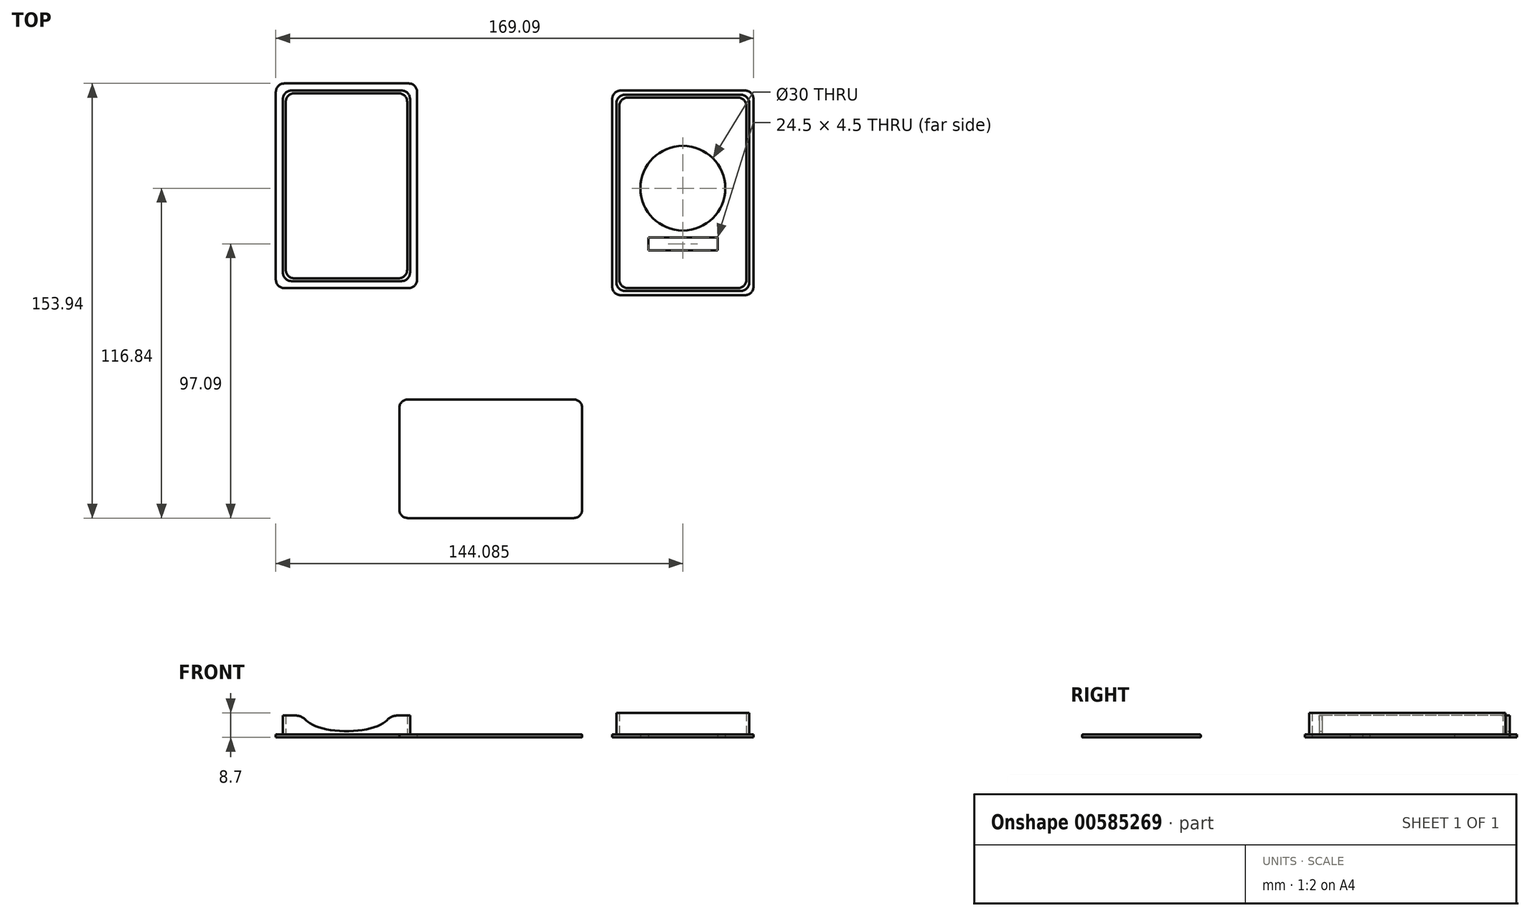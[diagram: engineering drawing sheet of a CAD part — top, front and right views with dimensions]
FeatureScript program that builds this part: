
annotation { "Feature Type Name" : "Feature", "Feature Type Description" : "" }
export const myFeature = defineFeature(function(context is Context, id is Id, definition is map)
    precondition{}
    {
        {
            var Q0;
            Q0=qCreatedBy(makeId("Top.planeOp"),FACE);
            var sketch = newSketch(context, id + "F0", { "sketchPlane" : qUnion([Q0])});
            skLineSegment(sketch, "E0.bottom", {"start": v(-88.15, 72.5) * mm, "end": v(-38.15, 72.5) * mm});
            skLineSegment(sketch, "E0.top", {"start": v(-88.15, 0) * mm, "end": v(-38.15, 0) * mm});
            skLineSegment(sketch, "E0.left", {"start": v(-88.15, 72.5) * mm, "end": v(-88.15, 0) * mm});
            skLineSegment(sketch, "E0.right", {"start": v(-38.15, 72.5) * mm, "end": v(-38.15, 0) * mm});
            skLineSegment(sketch, "E1.bottom", {"start": v(33.44, 67.5) * mm, "end": v(78.44, 67.5) * mm});
            skLineSegment(sketch, "E1.top", {"start": v(33.44, 0) * mm, "end": v(78.44, 0) * mm});
            skLineSegment(sketch, "E1.left", {"start": v(33.44, 67.5) * mm, "end": v(33.44, 0) * mm});
            skLineSegment(sketch, "E1.right", {"start": v(78.44, 67.5) * mm, "end": v(78.44, 0) * mm});
            skLineSegment(sketch, "E2.bottom", {"start": v(-44.44, -39.44) * mm, "end": v(20.3, -39.44) * mm});
            skLineSegment(sketch, "E2.top", {"start": v(-44.44, -81.44) * mm, "end": v(20.3, -81.44) * mm});
            skLineSegment(sketch, "E2.left", {"start": v(-44.44, -39.44) * mm, "end": v(-44.44, -81.44) * mm});
            skLineSegment(sketch, "E2.right", {"start": v(20.3, -39.44) * mm, "end": v(20.3, -81.44) * mm});
            skLineSegment(sketch, "E3.bottom", {"start": v(-40.65, 70) * mm, "end": v(-85.65, 70) * mm});
            skLineSegment(sketch, "E3.top", {"start": v(-40.65, 2.5) * mm, "end": v(-85.65, 2.5) * mm});
            skLineSegment(sketch, "E3.left", {"start": v(-40.65, 70) * mm, "end": v(-40.65, 2.5) * mm});
            skLineSegment(sketch, "E3.right", {"start": v(-85.65, 70) * mm, "end": v(-85.65, 2.5) * mm});
            skPoint(sketch, "E3.middle", {"position": v(-63.15, 36.25) * mm});
            skPoint(sketch, "E3.middle.positionSnap0", {"position": v(-88.15, 36.25) * mm});
            skPoint(sketch, "E3.middle.positionSnap1", {"position": v(-63.15, 72.5) * mm});
            skPoint(sketch, "E3.centerSnap0", {"position": v(-88.15, 36.25) * mm});
            skPoint(sketch, "E3.centerSnap1", {"position": v(-63.15, 72.5) * mm});
            skLineSegment(sketch, "E4.bottom", {"start": v(-41.65, 69) * mm, "end": v(-84.65, 69) * mm});
            skLineSegment(sketch, "E4.top", {"start": v(-41.65, 3.5) * mm, "end": v(-84.65, 3.5) * mm});
            skLineSegment(sketch, "E4.left", {"start": v(-41.65, 69) * mm, "end": v(-41.65, 3.5) * mm});
            skLineSegment(sketch, "E4.right", {"start": v(-84.65, 69) * mm, "end": v(-84.65, 3.5) * mm});
            skLineSegment(sketch, "E5.bottom", {"start": v(32.44, 68.5) * mm, "end": v(79.44, 68.5) * mm});
            skLineSegment(sketch, "E5.top", {"start": v(32.44, -1) * mm, "end": v(79.44, -1) * mm});
            skLineSegment(sketch, "E5.left", {"start": v(32.44, 68.5) * mm, "end": v(32.44, -1) * mm});
            skLineSegment(sketch, "E5.right", {"start": v(79.44, 68.5) * mm, "end": v(79.44, -1) * mm});
            skPoint(sketch, "E5.middle", {"position": v(55.94, 33.75) * mm});
            skPoint(sketch, "E5.middle.positionSnap0", {"position": v(55.94, 67.5) * mm});
            skPoint(sketch, "E5.middle.positionSnap1", {"position": v(33.44, 33.75) * mm});
            skPoint(sketch, "E5.centerSnap0", {"position": v(55.94, 67.5) * mm});
            skPoint(sketch, "E5.centerSnap1", {"position": v(33.44, 33.75) * mm});
            skLineSegment(sketch, "E6.bottom", {"start": v(80.94, -2.5) * mm, "end": v(30.94, -2.5) * mm});
            skLineSegment(sketch, "E6.top", {"start": v(80.94, 70) * mm, "end": v(30.94, 70) * mm});
            skLineSegment(sketch, "E6.left", {"start": v(80.94, -2.5) * mm, "end": v(80.94, 70) * mm});
            skLineSegment(sketch, "E6.right", {"start": v(30.94, -2.5) * mm, "end": v(30.94, 70) * mm});
            skCircle(sketch, "E7", {"center": v(55.94, 35.4) * mm, "radius": 15 * mm});
            skLineSegment(sketch, "E8.bottom", {"start": v(68.19, 17.9) * mm, "end": v(43.69, 17.9) * mm});
            skLineSegment(sketch, "E8.top", {"start": v(68.19, 13.4) * mm, "end": v(43.69, 13.4) * mm});
            skLineSegment(sketch, "E8.left", {"start": v(68.19, 17.9) * mm, "end": v(68.19, 13.4) * mm});
            skLineSegment(sketch, "E8.right", {"start": v(43.69, 17.9) * mm, "end": v(43.69, 13.4) * mm});
            skPoint(sketch, "E8.middle", {"position": v(55.94, 15.65) * mm});
            skSolve(sketch);
        }
        {
            var Q0;
            Q0=makeQuery(id+"F0.imprint","IMPRINT",FACE,{"disambiguationData":[TD([[makeQuery(id+"F0.imprint","IMPRINT",EDGE,{"derivedFrom":sQuery(id+"F0.wireOp",EDGE,"E2.bottom")}),-1.0]])]});
            extrude(context, id + "F1", {"entities" : qUnion([Q0]), "depth" : 1 * mm, "offsetDistance" : 25 * mm});
        }
        {
            var Q0;
            Q0=makeQuery(id+"F1.opExtrude","SWEPT_EDGE",EDGE,{"disambiguationData":[OSD([sQuery(id+"F0.wireOp",EDGE,"E2.bottom"),sQuery(id+"F0.wireOp",EDGE,"E2.left")])]});
            var Q1;
            Q1=makeQuery(id+"F1.opExtrude","SWEPT_EDGE",EDGE,{"disambiguationData":[OSD([sQuery(id+"F0.wireOp",EDGE,"E2.top"),sQuery(id+"F0.wireOp",EDGE,"E2.left")])]});
            var Q2;
            Q2=makeQuery(id+"F1.opExtrude","SWEPT_EDGE",EDGE,{"disambiguationData":[OSD([sQuery(id+"F0.wireOp",EDGE,"E2.top"),sQuery(id+"F0.wireOp",EDGE,"E2.right")])]});
            var Q3;
            Q3=makeQuery(id+"F1.opExtrude","SWEPT_EDGE",EDGE,{"disambiguationData":[OSD([sQuery(id+"F0.wireOp",EDGE,"E2.bottom"),sQuery(id+"F0.wireOp",EDGE,"E2.right")])]});
            fillet(context, id + "F2", {"entities" : qUnion([Q0, Q1, Q2, Q3]), "radius" : 3 * mm, "tangentPropagation" : true, "allowEdgeOverflow" : false});
        }
        {
            var Q0;
            Q0=makeQuery(id+"F1.opExtrude","CAP_FACE",FACE,{"disambiguationData":[OSD([sQuery(id+"F0.wireOp",EDGE,"E2.bottom"),sQuery(id+"F0.wireOp",EDGE,"E2.top"),sQuery(id+"F0.wireOp",EDGE,"E2.left"),sQuery(id+"F0.wireOp",EDGE,"E2.right")])],"isStart":false});
            var Q1;
            Q1=makeQuery(id+"F1.opExtrude","CAP_FACE",FACE,{"disambiguationData":[OSD([sQuery(id+"F0.wireOp",EDGE,"E2.bottom"),sQuery(id+"F0.wireOp",EDGE,"E2.top"),sQuery(id+"F0.wireOp",EDGE,"E2.left"),sQuery(id+"F0.wireOp",EDGE,"E2.right")])],"isStart":true});
            fillet(context, id + "F3", {"entities" : qUnion([Q0, Q1]), "radius" : 0.2 * mm, "tangentPropagation" : true, "allowEdgeOverflow" : false});
        }
        {
            var Q0;
            Q0=makeQuery(id+"F0.imprint","IMPRINT",FACE,{"disambiguationData":[TD([[makeQuery(id+"F0.imprint","IMPRINT",EDGE,{"derivedFrom":sQuery(id+"F0.wireOp",EDGE,"E0.bottom")}),-1.0]])]});
            var Q1;
            Q1=makeQuery(id+"F0.imprint","IMPRINT",FACE,{"disambiguationData":[TD([[makeQuery(id+"F0.imprint","IMPRINT",EDGE,{"derivedFrom":sQuery(id+"F0.wireOp",EDGE,"E3.bottom")}),1.0]])]});
            var Q2;
            Q2=makeQuery(id+"F0.imprint","IMPRINT",FACE,{"disambiguationData":[TD([[makeQuery(id+"F0.imprint","IMPRINT",EDGE,{"derivedFrom":sQuery(id+"F0.wireOp",EDGE,"E4.bottom")}),1.0]])]});
            extrude(context, id + "F4", {"entities" : qUnion([Q0, Q1, Q2]), "depth" : 1 * mm, "offsetDistance" : 25 * mm});
        }
        {
            var Q0;
            Q0=makeQuery(id+"F0.imprint","IMPRINT",FACE,{"disambiguationData":[TD([[makeQuery(id+"F0.imprint","IMPRINT",EDGE,{"derivedFrom":sQuery(id+"F0.wireOp",EDGE,"E3.bottom")}),1.0]])]});
            extrude(context, id + "F5", {"entities" : qUnion([Q0]), "operationType" : NewBodyOperationType.ADD, "depth" : 7.75 * mm, "offsetDistance" : 25 * mm});
        }
        {
            var Q0;
            Q0=makeQuery(id+"F5.opExtrude","SWEPT_EDGE",EDGE,{"disambiguationData":[OSD([sQuery(id+"F0.wireOp",EDGE,"E3.top"),sQuery(id+"F0.wireOp",EDGE,"E3.right")])]});
            var Q1;
            Q1=makeQuery(id+"F5.opExtrude","SWEPT_EDGE",EDGE,{"disambiguationData":[OSD([sQuery(id+"F0.wireOp",EDGE,"E3.top"),sQuery(id+"F0.wireOp",EDGE,"E3.left")])]});
            var Q2;
            Q2=makeQuery(id+"F5.opExtrude","SWEPT_EDGE",EDGE,{"disambiguationData":[OSD([sQuery(id+"F0.wireOp",EDGE,"E3.bottom"),sQuery(id+"F0.wireOp",EDGE,"E3.right")])]});
            var Q3;
            Q3=makeQuery(id+"F5.opExtrude","SWEPT_EDGE",EDGE,{"disambiguationData":[OSD([sQuery(id+"F0.wireOp",EDGE,"E3.bottom"),sQuery(id+"F0.wireOp",EDGE,"E3.left")])]});
            var Q4;
            Q4=makeQuery(id+"F4.opExtrude","SWEPT_EDGE",EDGE,{"disambiguationData":[OSD([sQuery(id+"F0.wireOp",EDGE,"E0.bottom"),sQuery(id+"F0.wireOp",EDGE,"E0.left")])]});
            var Q5;
            Q5=makeQuery(id+"F4.opExtrude","SWEPT_EDGE",EDGE,{"disambiguationData":[OSD([sQuery(id+"F0.wireOp",EDGE,"E0.bottom"),sQuery(id+"F0.wireOp",EDGE,"E0.right")])]});
            var Q6;
            Q6=makeQuery(id+"F4.opExtrude","SWEPT_EDGE",EDGE,{"disambiguationData":[OSD([sQuery(id+"F0.wireOp",EDGE,"E0.top"),sQuery(id+"F0.wireOp",EDGE,"E0.right")])]});
            var Q7;
            Q7=makeQuery(id+"F4.opExtrude","SWEPT_EDGE",EDGE,{"disambiguationData":[OSD([sQuery(id+"F0.wireOp",EDGE,"E0.top"),sQuery(id+"F0.wireOp",EDGE,"E0.left")])]});
            var Q8;
            Q8=makeQuery(id+"F5.opExtrude","SWEPT_EDGE",EDGE,{"disambiguationData":[OSD([sQuery(id+"F0.wireOp",EDGE,"E4.top"),sQuery(id+"F0.wireOp",EDGE,"E4.left")])]});
            var Q9;
            Q9=makeQuery(id+"F5.opExtrude","SWEPT_EDGE",EDGE,{"disambiguationData":[OSD([sQuery(id+"F0.wireOp",EDGE,"E4.top"),sQuery(id+"F0.wireOp",EDGE,"E4.right")])]});
            var Q10;
            Q10=makeQuery(id+"F5.opExtrude","SWEPT_EDGE",EDGE,{"disambiguationData":[OSD([sQuery(id+"F0.wireOp",EDGE,"E4.bottom"),sQuery(id+"F0.wireOp",EDGE,"E4.right")])]});
            var Q11;
            Q11=makeQuery(id+"F5.opExtrude","SWEPT_EDGE",EDGE,{"disambiguationData":[OSD([sQuery(id+"F0.wireOp",EDGE,"E4.bottom"),sQuery(id+"F0.wireOp",EDGE,"E4.left")])]});
            fillet(context, id + "F6", {"entities" : qUnion([Q0, Q1, Q2, Q3, Q4, Q5, Q6, Q7, Q8, Q9, Q10, Q11]), "radius" : 3 * mm, "tangentPropagation" : true, "allowEdgeOverflow" : false});
        }
        {
            var Q0;
            Q0=makeQuery(id+"F5.opExtrude","SWEPT_FACE",FACE,{"disambiguationData":[OSD([sQuery(id+"F0.wireOp",EDGE,"E3.top")])]});
            var sketch = newSketch(context, id + "F7", { "sketchPlane" : qUnion([Q0])});
            skEllipse(sketch, "E9", {"center": v(-63.15, 7.75) * mm, "majorRadius": 15 * mm, "minorRadius": 5.5 * mm, "majorAxis": v(1, 0)});
            skSolve(sketch);
        }
        {
            var Q0;
            Q0 = qSketchRegion(id + "F7", true);
            extrude(context, id + "F8", {"entities" : qUnion([Q0]), "operationType" : NewBodyOperationType.REMOVE, "endBound" : BoundingType.THROUGH_ALL, "oppositeDirection" : true, "depth" : 25 * mm, "offsetDistance" : 25 * mm});
        }
        {
            var Q0;
            Q0=makeQuery(id+"F8.boolean.opBoolean","INTERSECT",EDGE,{"disambiguationData":[OD(1.0)],"derivedFrom":[makeQuery(id+"F5.opExtrude","CAP_FACE",FACE,{"disambiguationData":[OSD([sQuery(id+"F0.wireOp",EDGE,"E3.bottom"),sQuery(id+"F0.wireOp",EDGE,"E3.top"),sQuery(id+"F0.wireOp",EDGE,"E3.left"),sQuery(id+"F0.wireOp",EDGE,"E3.right"),sQuery(id+"F0.wireOp",EDGE,"E4.bottom"),sQuery(id+"F0.wireOp",EDGE,"E4.top"),sQuery(id+"F0.wireOp",EDGE,"E4.left"),sQuery(id+"F0.wireOp",EDGE,"E4.right")])],"isStart":false}),makeQuery(id+"F8.opExtrude","SWEPT_FACE",FACE,{"disambiguationData":[OSD([sQuery(id+"F7.wireOp",EDGE,"E9")])]})]});
            var Q1;
            Q1=makeQuery(id+"F8.boolean.opBoolean","INTERSECT",EDGE,{"disambiguationData":[OD(3.0)],"derivedFrom":[makeQuery(id+"F5.opExtrude","CAP_FACE",FACE,{"disambiguationData":[OSD([sQuery(id+"F0.wireOp",EDGE,"E3.bottom"),sQuery(id+"F0.wireOp",EDGE,"E3.top"),sQuery(id+"F0.wireOp",EDGE,"E3.left"),sQuery(id+"F0.wireOp",EDGE,"E3.right"),sQuery(id+"F0.wireOp",EDGE,"E4.bottom"),sQuery(id+"F0.wireOp",EDGE,"E4.top"),sQuery(id+"F0.wireOp",EDGE,"E4.left"),sQuery(id+"F0.wireOp",EDGE,"E4.right")])],"isStart":false}),makeQuery(id+"F8.opExtrude","SWEPT_FACE",FACE,{"disambiguationData":[OSD([sQuery(id+"F7.wireOp",EDGE,"E9")])]})]});
            var Q2;
            Q2=makeQuery(id+"F8.boolean.opBoolean","INTERSECT",EDGE,{"disambiguationData":[OD(0.0)],"derivedFrom":[makeQuery(id+"F5.opExtrude","CAP_FACE",FACE,{"disambiguationData":[OSD([sQuery(id+"F0.wireOp",EDGE,"E3.bottom"),sQuery(id+"F0.wireOp",EDGE,"E3.top"),sQuery(id+"F0.wireOp",EDGE,"E3.left"),sQuery(id+"F0.wireOp",EDGE,"E3.right"),sQuery(id+"F0.wireOp",EDGE,"E4.bottom"),sQuery(id+"F0.wireOp",EDGE,"E4.top"),sQuery(id+"F0.wireOp",EDGE,"E4.left"),sQuery(id+"F0.wireOp",EDGE,"E4.right")])],"isStart":false}),makeQuery(id+"F8.opExtrude","SWEPT_FACE",FACE,{"disambiguationData":[OSD([sQuery(id+"F7.wireOp",EDGE,"E9")])]})]});
            var Q3;
            Q3=makeQuery(id+"F8.boolean.opBoolean","INTERSECT",EDGE,{"disambiguationData":[OD(2.0)],"derivedFrom":[makeQuery(id+"F5.opExtrude","CAP_FACE",FACE,{"disambiguationData":[OSD([sQuery(id+"F0.wireOp",EDGE,"E3.bottom"),sQuery(id+"F0.wireOp",EDGE,"E3.top"),sQuery(id+"F0.wireOp",EDGE,"E3.left"),sQuery(id+"F0.wireOp",EDGE,"E3.right"),sQuery(id+"F0.wireOp",EDGE,"E4.bottom"),sQuery(id+"F0.wireOp",EDGE,"E4.top"),sQuery(id+"F0.wireOp",EDGE,"E4.left"),sQuery(id+"F0.wireOp",EDGE,"E4.right")])],"isStart":false}),makeQuery(id+"F8.opExtrude","SWEPT_FACE",FACE,{"disambiguationData":[OSD([sQuery(id+"F7.wireOp",EDGE,"E9")])]})]});
            fillet(context, id + "F9", {"entities" : qUnion([Q0, Q1, Q2, Q3]), "radius" : 5 * mm, "tangentPropagation" : true, "allowEdgeOverflow" : false});
        }
        {
            var Q0;
            Q0=makeQuery(id+"F0.imprint","IMPRINT",FACE,{"disambiguationData":[TD([[makeQuery(id+"F0.imprint","IMPRINT",EDGE,{"derivedFrom":sQuery(id+"F0.wireOp",EDGE,"E5.bottom")}),1.0]])]});
            var Q1;
            Q1=makeQuery(id+"F0.imprint","IMPRINT",FACE,{"disambiguationData":[TD([[makeQuery(id+"F0.imprint","IMPRINT",EDGE,{"derivedFrom":sQuery(id+"F0.wireOp",EDGE,"E1.bottom")}),1.0]])]});
            var Q2;
            Q2=makeQuery(id+"F0.imprint","IMPRINT",FACE,{"disambiguationData":[TD([[makeQuery(id+"F0.imprint","IMPRINT",EDGE,{"derivedFrom":sQuery(id+"F0.wireOp",EDGE,"E1.bottom")}),-1.0]])]});
            extrude(context, id + "F10", {"entities" : qUnion([Q0, Q1, Q2]), "depth" : 1 * mm, "offsetDistance" : 25 * mm});
        }
        {
            var Q0;
            Q0=makeQuery(id+"F0.imprint","IMPRINT",FACE,{"disambiguationData":[TD([[makeQuery(id+"F0.imprint","IMPRINT",EDGE,{"derivedFrom":sQuery(id+"F0.wireOp",EDGE,"E1.bottom")}),1.0]])]});
            extrude(context, id + "F11", {"entities" : qUnion([Q0]), "operationType" : NewBodyOperationType.ADD, "depth" : 8.7 * mm, "offsetDistance" : 25 * mm});
        }
        {
            var Q0;
            Q0=makeQuery(id+"F10.opExtrude","SWEPT_EDGE",EDGE,{"disambiguationData":[OSD([sQuery(id+"F0.wireOp",EDGE,"E6.bottom"),sQuery(id+"F0.wireOp",EDGE,"E6.left")])]});
            var Q1;
            Q1=makeQuery(id+"F11.opExtrude","SWEPT_EDGE",EDGE,{"disambiguationData":[OSD([sQuery(id+"F0.wireOp",EDGE,"E5.top"),sQuery(id+"F0.wireOp",EDGE,"E5.right")])]});
            var Q2;
            Q2=makeQuery(id+"F11.opExtrude","SWEPT_EDGE",EDGE,{"disambiguationData":[OSD([sQuery(id+"F0.wireOp",EDGE,"E1.top"),sQuery(id+"F0.wireOp",EDGE,"E1.right")])]});
            var Q3;
            Q3=makeQuery(id+"F10.opExtrude","SWEPT_EDGE",EDGE,{"disambiguationData":[OSD([sQuery(id+"F0.wireOp",EDGE,"E6.bottom"),sQuery(id+"F0.wireOp",EDGE,"E6.right")])]});
            var Q4;
            Q4=makeQuery(id+"F11.opExtrude","SWEPT_EDGE",EDGE,{"disambiguationData":[OSD([sQuery(id+"F0.wireOp",EDGE,"E5.top"),sQuery(id+"F0.wireOp",EDGE,"E5.left")])]});
            var Q5;
            Q5=makeQuery(id+"F11.opExtrude","SWEPT_EDGE",EDGE,{"disambiguationData":[OSD([sQuery(id+"F0.wireOp",EDGE,"E1.top"),sQuery(id+"F0.wireOp",EDGE,"E1.left")])]});
            var Q6;
            Q6=makeQuery(id+"F11.opExtrude","SWEPT_EDGE",EDGE,{"disambiguationData":[OSD([sQuery(id+"F0.wireOp",EDGE,"E1.bottom"),sQuery(id+"F0.wireOp",EDGE,"E1.left")])]});
            var Q7;
            Q7=makeQuery(id+"F11.opExtrude","SWEPT_EDGE",EDGE,{"disambiguationData":[OSD([sQuery(id+"F0.wireOp",EDGE,"E1.bottom"),sQuery(id+"F0.wireOp",EDGE,"E1.right")])]});
            var Q8;
            Q8=makeQuery(id+"F11.opExtrude","SWEPT_EDGE",EDGE,{"disambiguationData":[OSD([sQuery(id+"F0.wireOp",EDGE,"E5.bottom"),sQuery(id+"F0.wireOp",EDGE,"E5.left")])]});
            var Q9;
            Q9=makeQuery(id+"F10.opExtrude","SWEPT_EDGE",EDGE,{"disambiguationData":[OSD([sQuery(id+"F0.wireOp",EDGE,"E6.top"),sQuery(id+"F0.wireOp",EDGE,"E6.right")])]});
            var Q10;
            Q10=makeQuery(id+"F10.opExtrude","SWEPT_EDGE",EDGE,{"disambiguationData":[OSD([sQuery(id+"F0.wireOp",EDGE,"E6.top"),sQuery(id+"F0.wireOp",EDGE,"E6.left")])]});
            var Q11;
            Q11=makeQuery(id+"F11.opExtrude","SWEPT_EDGE",EDGE,{"disambiguationData":[OSD([sQuery(id+"F0.wireOp",EDGE,"E5.bottom"),sQuery(id+"F0.wireOp",EDGE,"E5.right")])]});
            fillet(context, id + "F12", {"entities" : qUnion([Q0, Q1, Q2, Q3, Q4, Q5, Q6, Q7, Q8, Q9, Q10, Q11]), "radius" : 3 * mm, "tangentPropagation" : true, "allowEdgeOverflow" : false});
        }
    });
